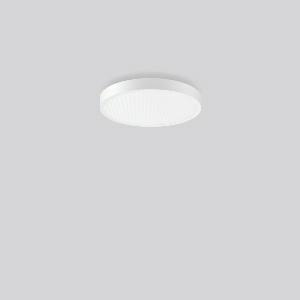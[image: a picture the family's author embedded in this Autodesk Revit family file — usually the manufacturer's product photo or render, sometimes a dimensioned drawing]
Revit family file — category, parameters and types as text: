
# Revit family: triona_round_a_312423_002_1_730_ea7a
name_source: partatom
category: Lighting Fixtures
units: mm (PartAtom-declared; Revit-internal decimal feet)

## family parameters
Cut with Voids When Loaded = No
Host = Face
Light Source = No
Part Type = Normal
Room Calculation Point = No
Round Connector Dimension = Use Diameter
Shared = No

## types (1)
- TRIONA round A (1 x LED Modul 840, 3250 lm, 4000)
    Apparent Load = 28 VA
    CIE Flux Codes = 58 87 97 100 100
    Color Rendering = 80
    Color Temperature = 4000
    Default Elevation = 1800 mm
    Description = Series: TRIONA round
Decorative round LED surface-mounted luminaire. Flat, seamless frame: aluminium extrusion profile, powder coated. Cover made of sheet steel, powder-coated. Light emission through a diffuser in plastic, opal/prismatic. Lightguide and diffuser made of non-yellowing plastic (PMMA). Lateral light emission (RZB SIDELITE technology) for above-average homogeneous light distribution. Suitable for Ceiling mounting, Wall (surface). Tool-free mounting via bayonet connection. Electronic ballast included. Very easy installation thanks to Plug+Play connection. With Casambi smart+free Bluetooth control for wireless network and operation using Android / iOS devices, free app available for download. Perfect for office areas (RUG < 19) and environments with computer screens in accordance with EN 12464-1. 
Colour: traffic white, matt (RAL 9016)
Diameter: 461 mm
Height: 88 mm
Lamp: LED
Socket: without socket
Colour temperature: 4000K
Colour rendering index (CRI): 80
System power: 28 W
Rated luminous flux: 3250 lm
Luminous efficiency: 116 lm/W
Control gear: Dimmable Bluetooth converter
Protection class: I
Type of protection: IP 20
    Height = 88 mm
    Lamp = 1 x LED Modul 840
    Lamp Light Flux = 3250 lm
    Lamp count = 1
    Length = 461 mm
    Lifetime = 50000 h
    Luminous efficacy = 116 lm/W
    Manufacturer = RZB
    ModVariant = No
    Model = 312423.002.1.730
    Mounting Place = Ceiling
    Mounting Type = Surface mounted
    Number of Poles = 1
    OnlyDefault = Yes
    Power Factor = 1
    Product Name = TRIONA round A
    Product group = Surface mounted modular luminaires
    ProductGroupID = 306
    Protection Class = Protection class I
    Protection Degree = IP 20
    RLX_Detail_Level = 1
    RLX_Emergency_Light_Flux = 0 lm
    RLX_Emergency_Type = 0
    RLX_Emergency_Type_DB = No
    RlxData = <blob elided: 27969 chars, md5=185804d7>
    Socket = socket
    Standby Power = 0 W
    System Light Flux = 3250 lm
    System Power = 28 W
    Type Comments = Product without accessories
    Type Image = 312424.002.jpg
    URL = http://relux.com
    VarID = ---
    Voltage = 230 V
    Voltage Range = 220-240 V
    Weight = 0.00 kg
    Width = 0 mm  [stored 0 ft]

note: [stored X ft] marks values corroborated as IEEE doubles in the binary element streams (Revit-internal decimal feet)

## geometry (parser evidence)
native form markers: Blend x4, Sweep x12
no freeform markers — native parametric forms only
